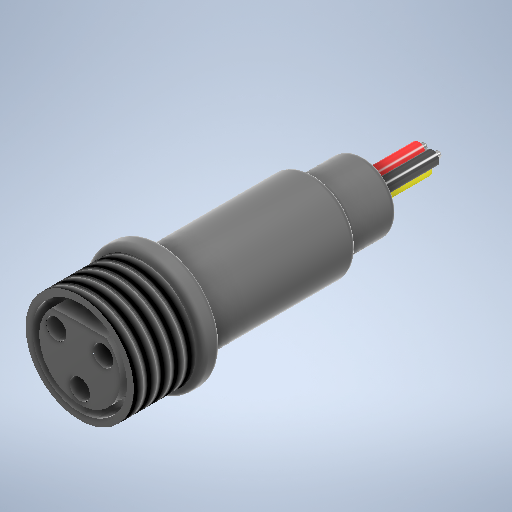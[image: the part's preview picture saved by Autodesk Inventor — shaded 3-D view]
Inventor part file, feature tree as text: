
AUTODESK INVENTOR PART (.ipt)
format: ipt  version: 2025 (Build 290162000, 162)  size: 396,800 bytes
history: native  units: in
note: dims shown in document units (in); Inventor stores cm internally (conversion verified against a paired STEP export)
features: sketch x10, extrude x8, fillet x3, thread x1, projected_geometry x1
ambient origin geometry x8: Origin, YZ Plane, XZ Plane, XY Plane, X Axis, Y Axis, Z Axis, Center Point
bodies: Solid1 (feature_tree)
feature tree (23):
  extrude  "Extrusion1"  Depth=0.8858in TaperAngle=0.0deg
  extrude  "Extrusion2"  Depth=0.0394in TaperAngle=0.0deg
  fillet  "Fillet1"  Radius=0.0394in
  extrude  "Extrusion3"  Depth=0.1181in TaperAngle=0.0deg
  extrude  "Extrusion4"  Depth=0.3622in TaperAngle=0.0deg
  fillet  "Fillet2"  Radius=0.0394in
  thread  "Thread1"  [1 undecoded]
  extrude  "Extrusion5"  Depth=0.1181in
  extrude  "Extrusion6"  Depth=0.3622in TaperAngle=0.0deg
  extrude  "Extrusion7"  Depth=1.1811in
  fillet  "Fillet3"  Radius=1.1811in
  extrude  "Extrusion8"  Depth=0.0394in
  sketch  "Sketch1"  dims[d0=0.5118in d1=0.8858in d2=0.0in]
  sketch  "Sketch2"  dims[d7=0.7008in d8=0.1181in d9=0.0in]
  sketch  "Sketch3"  dims[d16=0.315in d17=0.1181in]
  sketch  "Sketch4"  dims[d18=1.1811in d20=360.0deg d22=0.3622in d23=0.0in]
  sketch  "Sketch5"  dims[d24=0.0472in d25=0.0787in d26=1.1811in d28=360.0deg]
  sketch  "Sketch Circular Pattern1"  dims[d3=0.3937in d4=0.2953in d5=0.0in d6=0.0394in]
  sketch  "Sketch6"  dims[d30=0.3937in d31=0.0in d32=0.0394in]
  sketch  "Sketch Circular Pattern2"  dims[d10=0.6299in d11=0.3622in d12=0.0in d13=0.0394in d14=0.3622in d15=0.0in]
  sketch  "Sketch7"  dims[d33=0.0394in]
  projected_geometry  "Projected Loop1"
  sketch  "Sketch8"  dims[d34=0.0394in d35=0.0394in d36=0.0in d37=0.0098in d38=0.4724in d39=0.5512in d41=0.2362in d42=0.0in]
note: 1 required parameter value undecoded (feature->parameter linkage not recoverable at this tier; creation-order binding heuristic only, values carry confidence <= 0.55)
